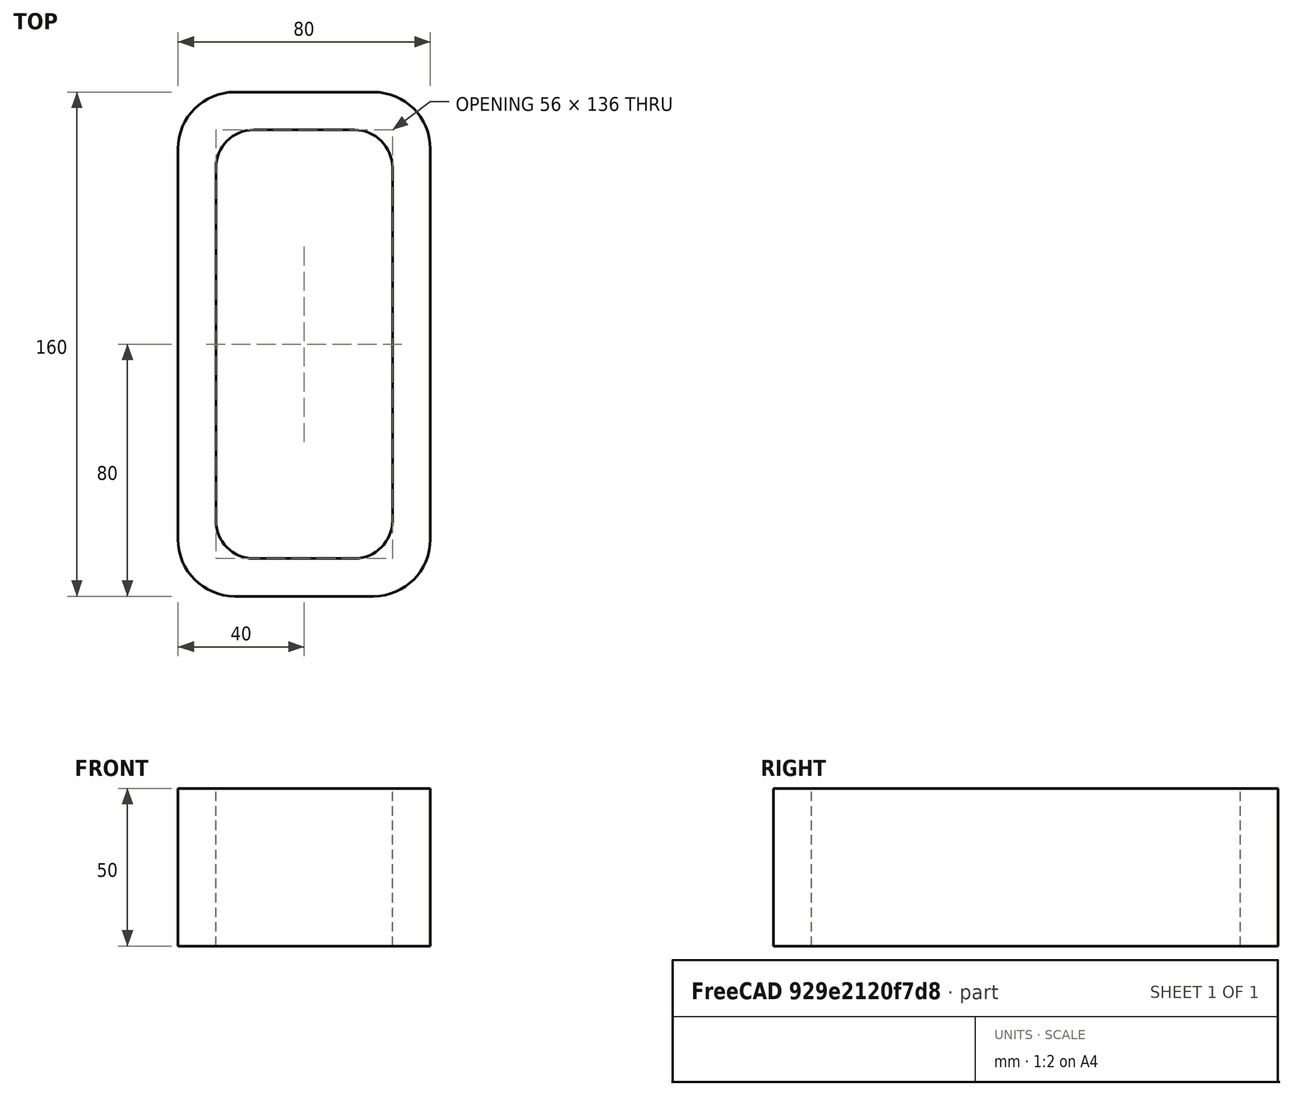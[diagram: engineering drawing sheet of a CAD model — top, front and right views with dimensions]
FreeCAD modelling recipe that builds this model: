
FCSTD DOCUMENT  (FreeCAD 0.15R4671 (Git))
Label: Rectangular hollow section 160x80x12 EN10219 S235JRH
License: All rights reserved
LicenseURL: http://en.wikipedia.org/wiki/All_rights_reserved
objects: Sketcher::SketchObject×1, Part::Extrusion×1
note: 2 computed .brp shape members not serialized (recipe doc carries the construction recipe); baked Part::Feature solids carry a one-line shape summary decoded from their .brp

FEATURE [Sketcher::SketchObject] Sketch
  sketch-geometry (16):
    g0: LineSegment StartX=-16 StartY=68 StartZ=0 EndX=16 EndY=68 EndZ=0
    g1: LineSegment StartX=28 StartY=56 StartZ=0 EndX=28 EndY=-56 EndZ=0
    g2: LineSegment StartX=16 StartY=-68 StartZ=0 EndX=-16 EndY=-68 EndZ=0
    g3: LineSegment StartX=-28 StartY=-56 StartZ=0 EndX=-28 EndY=56 EndZ=0
    g4: LineSegment StartX=-22 StartY=80 StartZ=0 EndX=22 EndY=80 EndZ=0
    g5: LineSegment StartX=40 StartY=62 StartZ=0 EndX=40 EndY=-62 EndZ=0
    g6: LineSegment StartX=22 StartY=-80 StartZ=0 EndX=-22 EndY=-80 EndZ=0
    g7: LineSegment StartX=-40 StartY=-62 StartZ=0 EndX=-40 EndY=62 EndZ=0
    g8: ArcOfCircle CenterX=-16 CenterY=56 CenterZ=0 NormalX=0 NormalY=0 NormalZ=1 Radius=12 StartAngle=1.5708 EndAngle=3.14159
    g9: ArcOfCircle CenterX=16 CenterY=56 CenterZ=0 NormalX=0 NormalY=0 NormalZ=1 Radius=12 StartAngle=0 EndAngle=1.5708
    g10: ArcOfCircle CenterX=16 CenterY=-56 CenterZ=0 NormalX=0 NormalY=0 NormalZ=1 Radius=12 StartAngle=4.71239 EndAngle=6.28319
    g11: ArcOfCircle CenterX=-16 CenterY=-56 CenterZ=0 NormalX=0 NormalY=0 NormalZ=1 Radius=12 StartAngle=3.14159 EndAngle=4.71239
    g12: ArcOfCircle CenterX=22 CenterY=62 CenterZ=0 NormalX=0 NormalY=0 NormalZ=1 Radius=18 StartAngle=0 EndAngle=1.5708
    g13: ArcOfCircle CenterX=22 CenterY=-62 CenterZ=0 NormalX=0 NormalY=0 NormalZ=1 Radius=18 StartAngle=4.71239 EndAngle=6.28319
    g14: ArcOfCircle CenterX=-22 CenterY=-62 CenterZ=0 NormalX=0 NormalY=0 NormalZ=1 Radius=18 StartAngle=3.14159 EndAngle=4.71239
    g15: ArcOfCircle CenterX=-22 CenterY=62 CenterZ=0 NormalX=0 NormalY=0 NormalZ=1 Radius=18 StartAngle=1.5708 EndAngle=3.14159
  constraints (36):
    c: Horizontal(g2)
    c: Vertical(g3)
    c: Horizontal(g6)
    c: Vertical(g7)
    c: Tangent(g3,g8) = 1.5708
    c: Tangent(g0,g8) = 1.5708
    c: Tangent(g0,g9) = 1.5708
    c: Tangent(g1,g9) = 1.5708
    c: Tangent(g1,g10) = 1.5708
    c: Tangent(g2,g10) = 1.5708
    c: Tangent(g2,g11) = 1.5708
    c: Tangent(g3,g11) = 1.5708
    c: Tangent(g4,g12) = 1.5708
    c: Tangent(g5,g12) = 1.5708
    c: Tangent(g5,g13) = 1.5708
    c: Tangent(g6,g13) = 1.5708
    c: Tangent(g6,g14) = 1.5708
    c: Tangent(g7,g14) = 1.5708
    c: Tangent(g7,g15) = 1.5708
    c: Tangent(g4,g15) = 1.5708
    c: Equal(g9,g8)
    c: Equal(g9,g11)
    c: Equal(g9,g10)
    c: Equal(g12,g15)
    c: Equal(g12,g14)
    c: Equal(g12,g13)
    c: Symmetric(g4,g6,g-1)
    c: Symmetric(g7,g5,g-2)
    c: DistanceY(g4,g6) = -160
    c: DistanceX(g7,g5) = 80
    c: Symmetric(g3,g1,g-2)
    c: Symmetric(g0,g2,g-1)
    c: DistanceY(g0,g4) = 12
    c: DistanceX(g5,g1) = -12
    c: Radius(g9) = 12
    c: Radius(g12) = 18
FEATURE [Part::Extrusion] Extrude  label="Rectangular hollow section 160x80x12 EN10219 S235JRH"
  Base = -> Sketch
  Dir = (0,0,50)
  Solid = true
